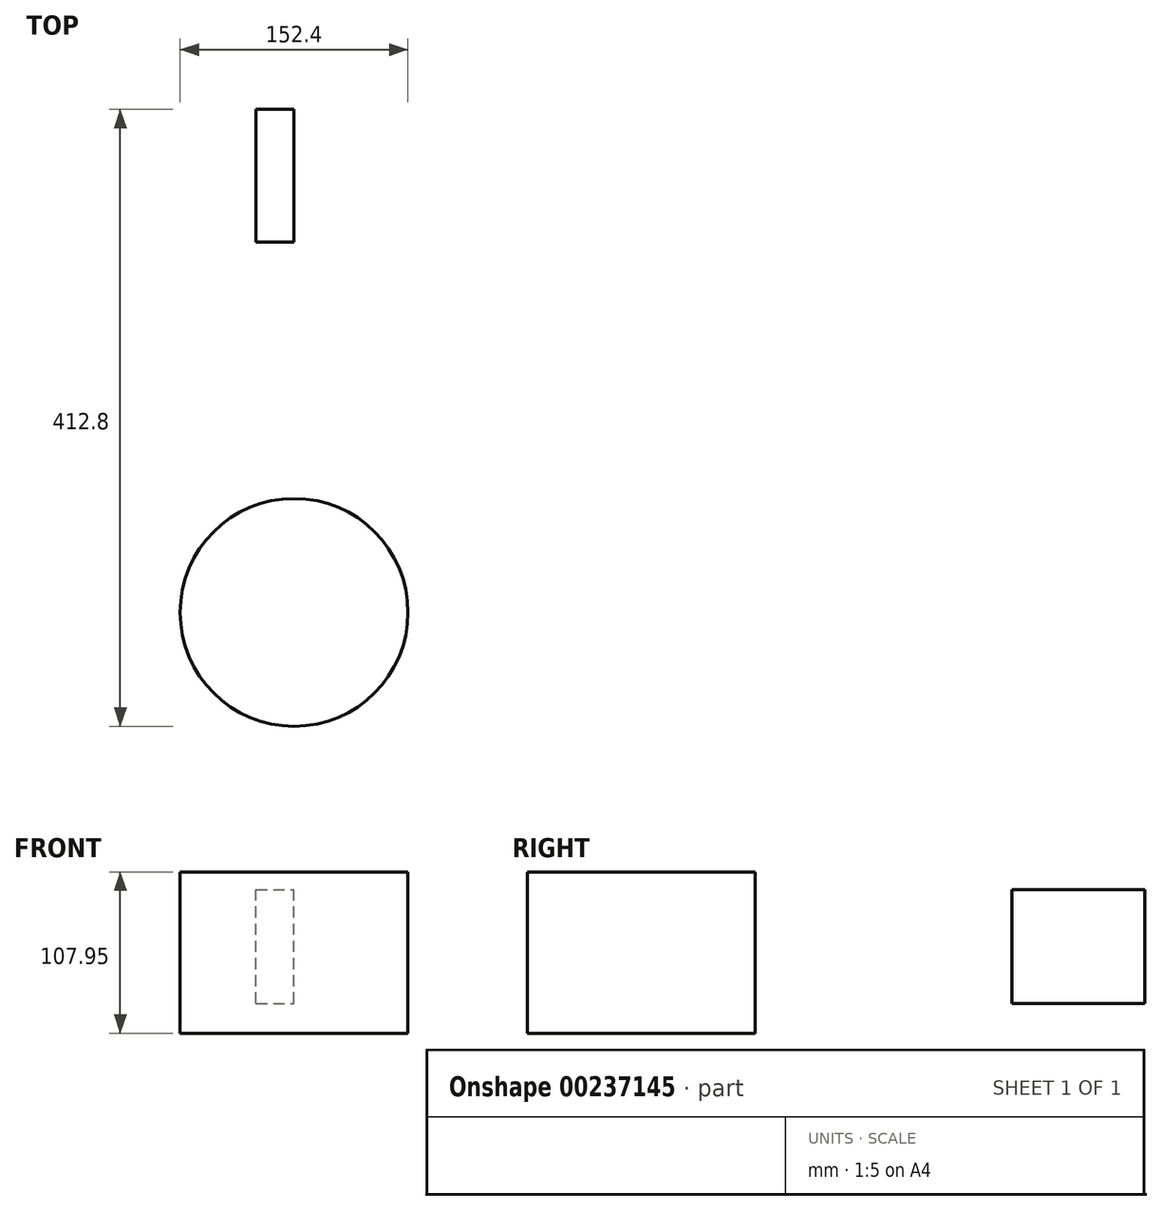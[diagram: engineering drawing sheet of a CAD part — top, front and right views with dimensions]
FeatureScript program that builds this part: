
annotation { "Feature Type Name" : "Feature", "Feature Type Description" : "" }
export const myFeature = defineFeature(function(context is Context, id is Id, definition is map)
    precondition{}
    {
        {
            var Q0;
            Q0=qCreatedBy(makeId("Top.planeOp"),FACE);
            var sketch = newSketch(context, id + "F0", { "sketchPlane" : qUnion([Q0])});
            skCircle(sketch, "E0", {"center": v(0, 0) * mm, "radius": 76.2 * mm});
            skLineSegment(sketch, "E1", {"start": v(0, 0) * mm, "end": v(-47, -59.98) * mm});
            skSolve(sketch);
        }
        {
            var Q0;
            Q0 = qSketchRegion(id + "F0", true);
            extrude(context, id + "F1", {"entities" : qUnion([Q0]), "depth" : 107.95 * mm});
        }
        {
            var Q0;
            Q0=qCreatedBy(makeId("Right.planeOp"),FACE);
            var sketch = newSketch(context, id + "F2", { "sketchPlane" : qUnion([Q0])});
            skLineSegment(sketch, "E2.bottom", {"start": v(247.7, 19.85) * mm, "end": v(336.6, 19.85) * mm});
            skLineSegment(sketch, "E2.top", {"start": v(247.7, 96.05) * mm, "end": v(336.6, 96.05) * mm});
            skLineSegment(sketch, "E2.left", {"start": v(247.7, 19.85) * mm, "end": v(247.7, 96.05) * mm});
            skLineSegment(sketch, "E2.right", {"start": v(336.6, 19.85) * mm, "end": v(336.6, 96.05) * mm});
            skSolve(sketch);
        }
        {
            var Q0;
            Q0 = qSketchRegion(id + "F2", true);
            extrude(context, id + "F3", {"entities" : qUnion([Q0]), "oppositeDirection" : true, "depth" : 25.4 * mm});
        }
    });
